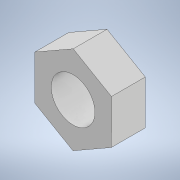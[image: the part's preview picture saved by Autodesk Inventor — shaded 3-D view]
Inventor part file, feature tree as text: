
AUTODESK INVENTOR PART (.ipt)
format: ipt  version: 2021 (Build 250183000, 183)  size: 99,840 bytes
history: native  units: mm
features: extrude x1, sketch x1
ambient origin geometry x8: Origin, YZ Plane, XZ Plane, XY Plane, X Axis, Y Axis, Z Axis, Center Point
bodies: Solid1 (feature_tree)
feature tree (2):
  extrude  "Extrusion1"  Depth=3.1mm
  sketch  "Sketch1"  dims[d0=3.5mm d1=4.0mm d2=3.1mm d3=0.0mm]
